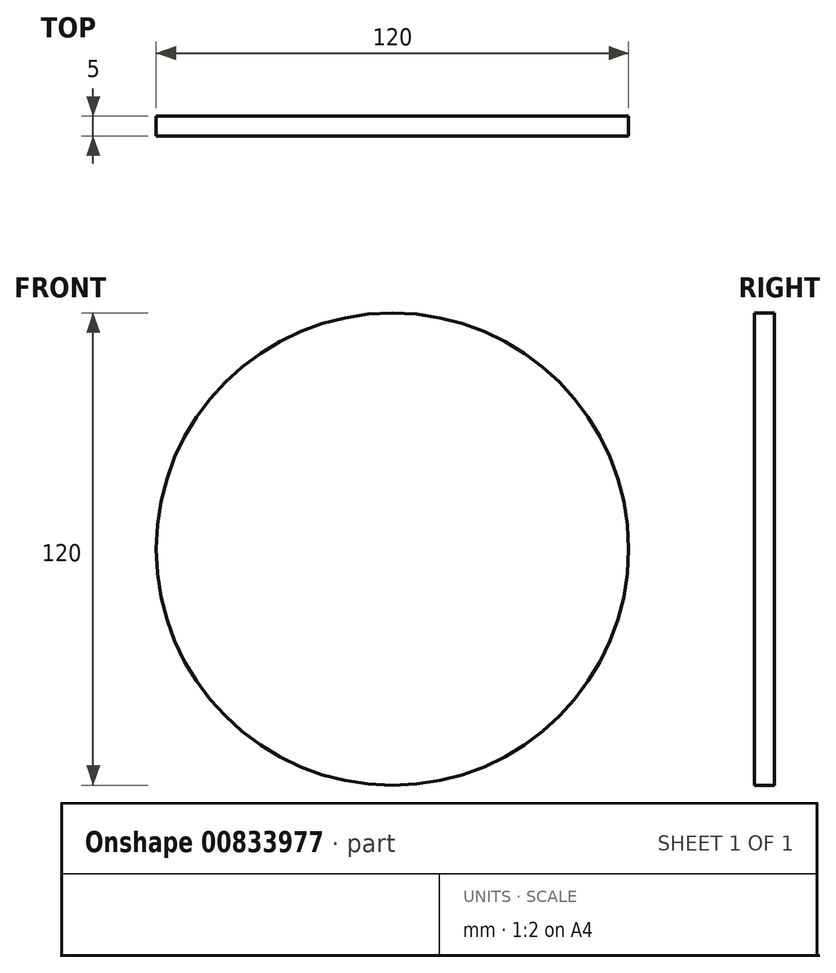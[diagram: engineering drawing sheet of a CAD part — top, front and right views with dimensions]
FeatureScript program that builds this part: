
annotation { "Feature Type Name" : "Feature", "Feature Type Description" : "" }
export const myFeature = defineFeature(function(context is Context, id is Id, definition is map)
    precondition{}
    {
        {
            var Q0;
            Q0=qCreatedBy(makeId("Front.planeOp"),FACE);
            var sketch = newSketch(context, id + "F0", { "sketchPlane" : qUnion([Q0])});
            skCircle(sketch, "E0", {"center": v(0, 0) * mm, "radius": 60 * mm});
            skSolve(sketch);
        }
        {
            var Q0;
            Q0=makeQuery(id+"F0.imprint","IMPRINT",FACE,{"disambiguationData":[TD([[makeQuery(id+"F0.imprint","IMPRINT",EDGE,{"derivedFrom":sQuery(id+"F0.wireOp",EDGE,"E0")}),1.0]])]});
            extrude(context, id + "F1", {"entities" : qUnion([Q0]), "depth" : 5 * mm, "offsetDistance" : 25 * mm});
        }
    });
